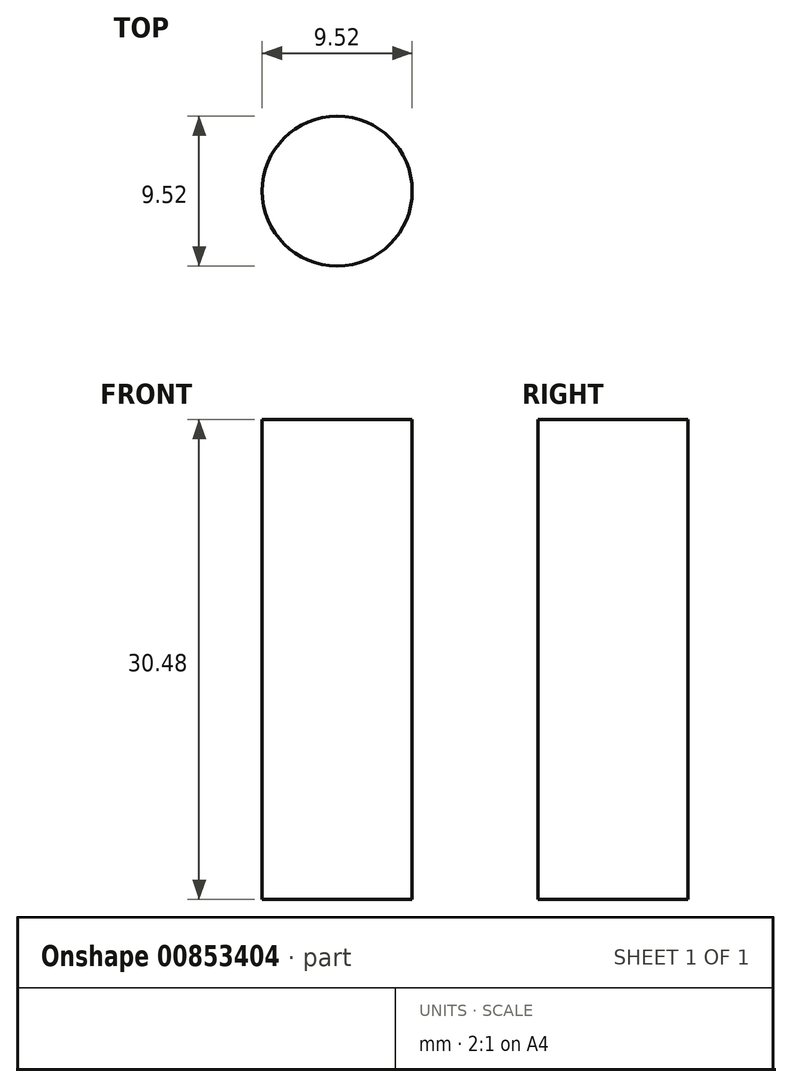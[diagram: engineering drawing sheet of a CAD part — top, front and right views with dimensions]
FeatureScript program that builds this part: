
annotation { "Feature Type Name" : "Feature", "Feature Type Description" : "" }
export const myFeature = defineFeature(function(context is Context, id is Id, definition is map)
    precondition{}
    {
        {
            var Q0;
            Q0=qCreatedBy(makeId("Top.planeOp"),FACE);
            var sketch = newSketch(context, id + "F0", { "sketchPlane" : qUnion([Q0])});
            skCircle(sketch, "E0", {"center": v(0, 0) * mm, "radius": 4.76 * mm});
            skSolve(sketch);
        }
        {
            var Q0;
            Q0 = qSketchRegion(id + "F0", true);
            extrude(context, id + "F1", {"entities" : qUnion([Q0]), "depth" : 30.48 * mm, "offsetDistance" : 25.4 * mm});
        }
    });
